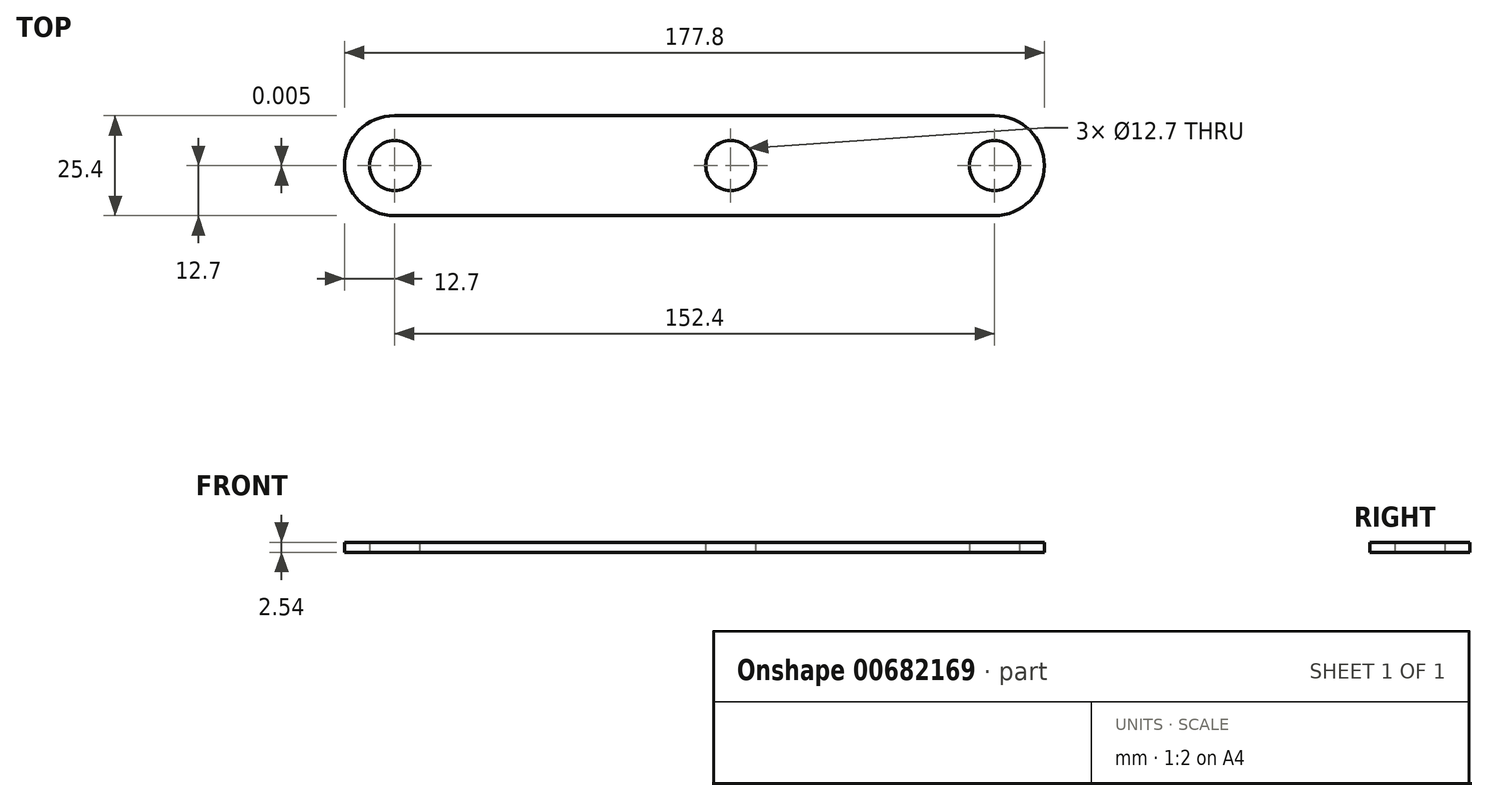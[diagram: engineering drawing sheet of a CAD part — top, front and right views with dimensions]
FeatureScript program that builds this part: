
annotation { "Feature Type Name" : "Feature", "Feature Type Description" : "" }
export const myFeature = defineFeature(function(context is Context, id is Id, definition is map)
    precondition{}
    {
        {
            var Q0;
            Q0=qCreatedBy(makeId("Top.planeOp"),FACE);
            var sketch = newSketch(context, id + "F0", { "sketchPlane" : qUnion([Q0]), "disableImprinting" : false});
            skLineSegment(sketch, "E0", {"start": v(0, 0) * mm, "end": v(-152.4, 0) * mm, "construction": true});
            skLineSegment(sketch, "E1.bottom", {"start": v(0, -12.7) * mm, "end": v(-152.4, -12.7) * mm});
            skLineSegment(sketch, "E1.top", {"start": v(0, 12.7) * mm, "end": v(-152.4, 12.7) * mm});
            skPoint(sketch, "E1.middle", {"position": v(-76.2, 0) * mm});
            skArc(sketch, "E2", {"start": v(-152.4, -12.7) * mm, "mid": v(-165.1, 0) * mm, "end": v(-152.4, 12.7) * mm});
            skArc(sketch, "E3", {"start": v(0, 12.7) * mm, "mid": v(12.7, 0) * mm, "end": v(0, -12.7) * mm});
            skCircle(sketch, "E4", {"center": v(-152.4, 0) * mm, "radius": 6.35 * mm});
            skCircle(sketch, "E5", {"center": v(0, 0) * mm, "radius": 6.35 * mm});
            skCircle(sketch, "E6", {"center": v(-66.99, 0) * mm, "radius": 6.35 * mm});
            skSolve(sketch);
        }
        {
            var Q0;
            Q0=makeQuery(id+"F0.imprint","IMPRINT",FACE,{"disambiguationData":[TD([[makeQuery(id+"F0.imprint","IMPRINT",EDGE,{"derivedFrom":sQuery(id+"F0.wireOp",EDGE,"E1.bottom")}),-1.0]])]});
            extrude(context, id + "F1", {"entities" : qUnion([Q0]), "depth" : 2.54 * mm, "offsetDistance" : 25.4 * mm});
        }
    });
